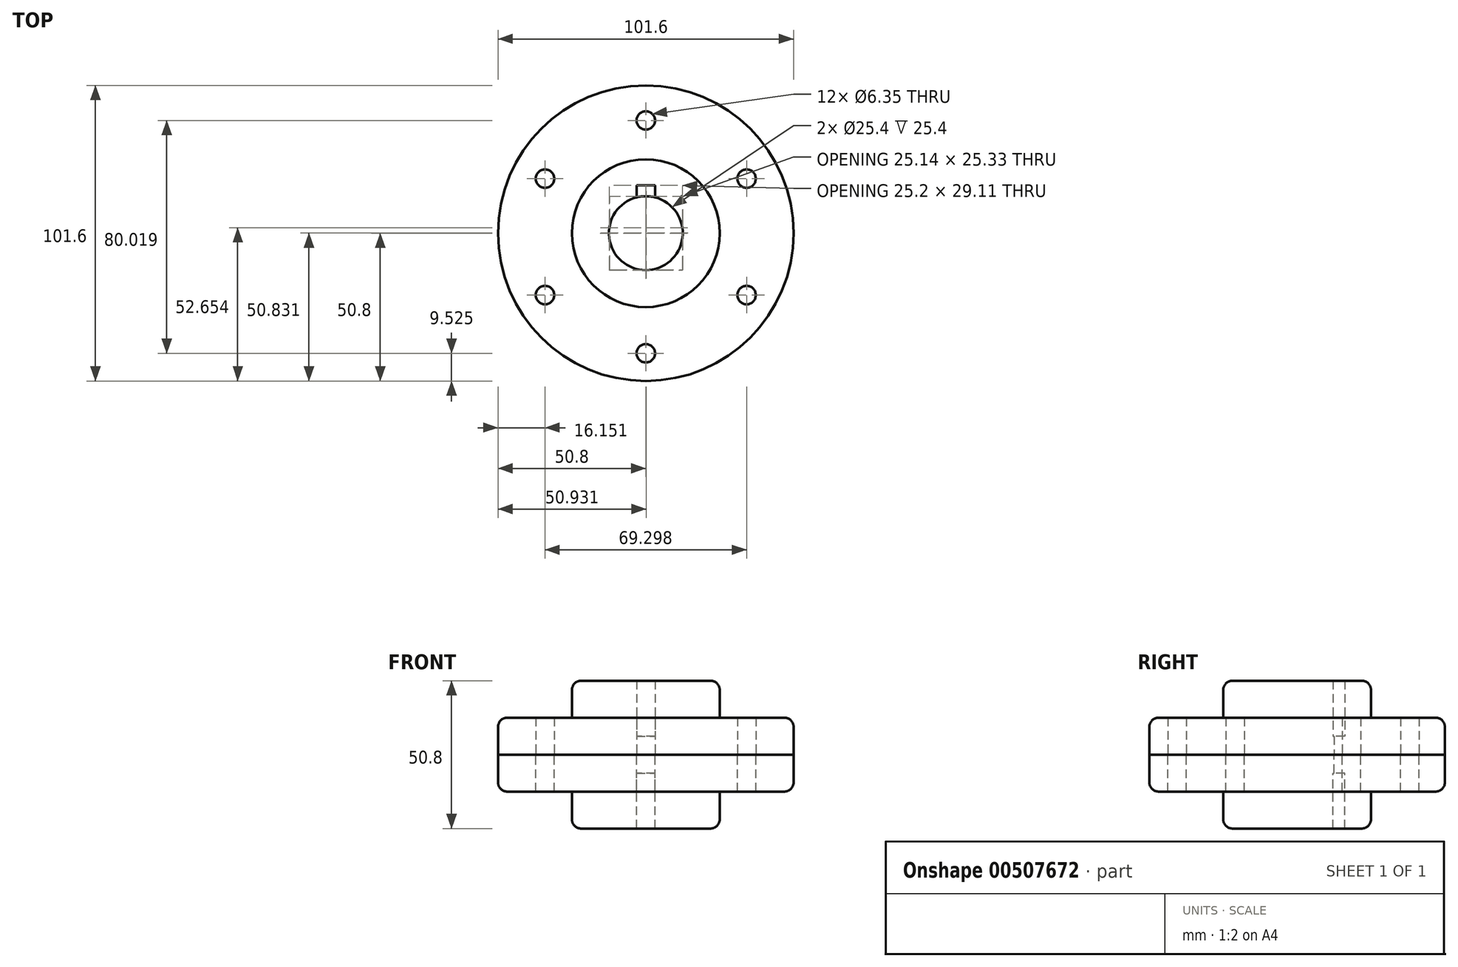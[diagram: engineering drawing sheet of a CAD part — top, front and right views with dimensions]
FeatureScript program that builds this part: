
annotation { "Feature Type Name" : "Feature", "Feature Type Description" : "" }
export const myFeature = defineFeature(function(context is Context, id is Id, definition is map)
    precondition{}
    {
        {
            var Q0;
            Q0=qCreatedBy(makeId("Top.planeOp"),FACE);
            var sketch = newSketch(context, id + "F0", { "sketchPlane" : qUnion([Q0])});
            skCircle(sketch, "E0", {"center": v(0, 0) * mm, "radius": 50.8 * mm});
            skCircle(sketch, "E1", {"center": v(0, 38.74) * mm, "radius": 3.18 * mm});
            skArc(sketch, "E2", {"start": v(-3.17, 12.3) * mm, "mid": v(0, -12.7) * mm, "end": v(3.17, 12.3) * mm});
            skCircle(sketch, "E3", {"center": v(0, 0) * mm, "radius": 25.4 * mm});
            skCircle(sketch, "E4.1.0", {"center": v(-34.65, 18.74) * mm, "radius": 3.18 * mm});
            skCircle(sketch, "E4.2.0", {"center": v(-34.65, -21.27) * mm, "radius": 3.18 * mm});
            skPoint(sketch, "E4.center", {"position": v(0, -1.27) * mm});
            skCircle(sketch, "E5.1.3.0", {"center": v(0, -41.28) * mm, "radius": 3.18 * mm});
            skCircle(sketch, "E5.1.4.0", {"center": v(34.65, -21.27) * mm, "radius": 3.18 * mm});
            skCircle(sketch, "E5.1.5.0", {"center": v(34.65, 18.74) * mm, "radius": 3.18 * mm});
            skLineSegment(sketch, "E6", {"start": v(0, 16.4) * mm, "end": v(3.17, 16.4) * mm});
            skLineSegment(sketch, "E7", {"start": v(0, 16.4) * mm, "end": v(-3.18, 16.4) * mm});
            skLineSegment(sketch, "E8", {"start": v(-3.18, 16.4) * mm, "end": v(-3.18, 12.3) * mm});
            skLineSegment(sketch, "E9", {"start": v(3.17, 16.4) * mm, "end": v(3.17, 12.3) * mm});
            skArc(sketch, "E10", {"start": v(3.18, 12.3) * mm, "mid": v(0, 12.7) * mm, "end": v(-3.17, 12.3) * mm});
            skSolve(sketch);
        }
        {
            var Q0;
            Q0=makeQuery(id+"F0.imprint","IMPRINT",FACE,{"disambiguationData":[TD([[makeQuery(id+"F0.imprint","IMPRINT",EDGE,{"derivedFrom":sQuery(id+"F0.wireOp",EDGE,"E2")}),-1.0]])]});
            var Q1;
            Q1=makeQuery(id+"F0.imprint","IMPRINT",FACE,{"disambiguationData":[TD([[makeQuery(id+"F0.imprint","IMPRINT",EDGE,{"derivedFrom":sQuery(id+"F0.wireOp",EDGE,"E0")}),1.0]])]});
            extrude(context, id + "F1", {"entities" : qUnion([Q0, Q1]), "depth" : 12.7 * mm});
        }
        {
            var Q0;
            Q0=makeQuery(id+"F0.imprint","IMPRINT",FACE,{"disambiguationData":[TD([[makeQuery(id+"F0.imprint","IMPRINT",EDGE,{"derivedFrom":sQuery(id+"F0.wireOp",EDGE,"E2")}),-1.0]])]});
            extrude(context, id + "F2", {"entities" : qUnion([Q0]), "operationType" : NewBodyOperationType.ADD, "depth" : 25.4 * mm});
        }
        {
            var Q0;
            Q0=makeQuery(id+"F2.opExtrude","CAP_EDGE",EDGE,{"disambiguationData":[OSD([sQuery(id+"F0.wireOp",EDGE,"E3")])],"isStart":false});
            var Q1;
            Q1=makeQuery(id+"F1.opExtrude","CAP_EDGE",EDGE,{"disambiguationData":[OSD([sQuery(id+"F0.wireOp",EDGE,"E0")])],"isStart":false});
            fillet(context, id + "F3", {"entities" : qUnion([Q0, Q1]), "radius" : 3.17 * mm, "tangentPropagation" : true, "allowEdgeOverflow" : false});
        }
        {
            var Q0;
            Q0=makeQuery(id+"F0.imprint","IMPRINT",FACE,{"disambiguationData":[TD([[makeQuery(id+"F0.imprint","IMPRINT",EDGE,{"derivedFrom":sQuery(id+"F0.wireOp",EDGE,"E6")}),-1.0]])]});
            extrude(context, id + "F4", {"entities" : qUnion([Q0]), "operationType" : NewBodyOperationType.ADD, "depth" : 6.35 * mm});
        }
        {
            var Q0;
            Q0=makeQuery(id+"F1.opExtrude","SWEPT_BODY",BODY,{"disambiguationData":[OSD([sQuery(id+"F0.wireOp",EDGE,"E0"),sQuery(id+"F0.wireOp",EDGE,"E1"),sQuery(id+"F0.wireOp",EDGE,"E2"),sQuery(id+"F0.wireOp",EDGE,"E4.1.0"),sQuery(id+"F0.wireOp",EDGE,"E4.2.0"),sQuery(id+"F0.wireOp",EDGE,"E5.1.3.0"),sQuery(id+"F0.wireOp",EDGE,"E5.1.4.0"),sQuery(id+"F0.wireOp",EDGE,"E5.1.5.0"),sQuery(id+"F0.wireOp",EDGE,"E6"),sQuery(id+"F0.wireOp",EDGE,"E7"),sQuery(id+"F0.wireOp",EDGE,"E8"),sQuery(id+"F0.wireOp",EDGE,"E9")])]});
            var Q1;
            Q1=qCreatedBy(makeId("Top.planeOp"),FACE);
            mirror(context, id + "F5", {"entities" : qUnion([Q0]), "mirrorPlane" : qUnion([Q1])});
        }
    });
